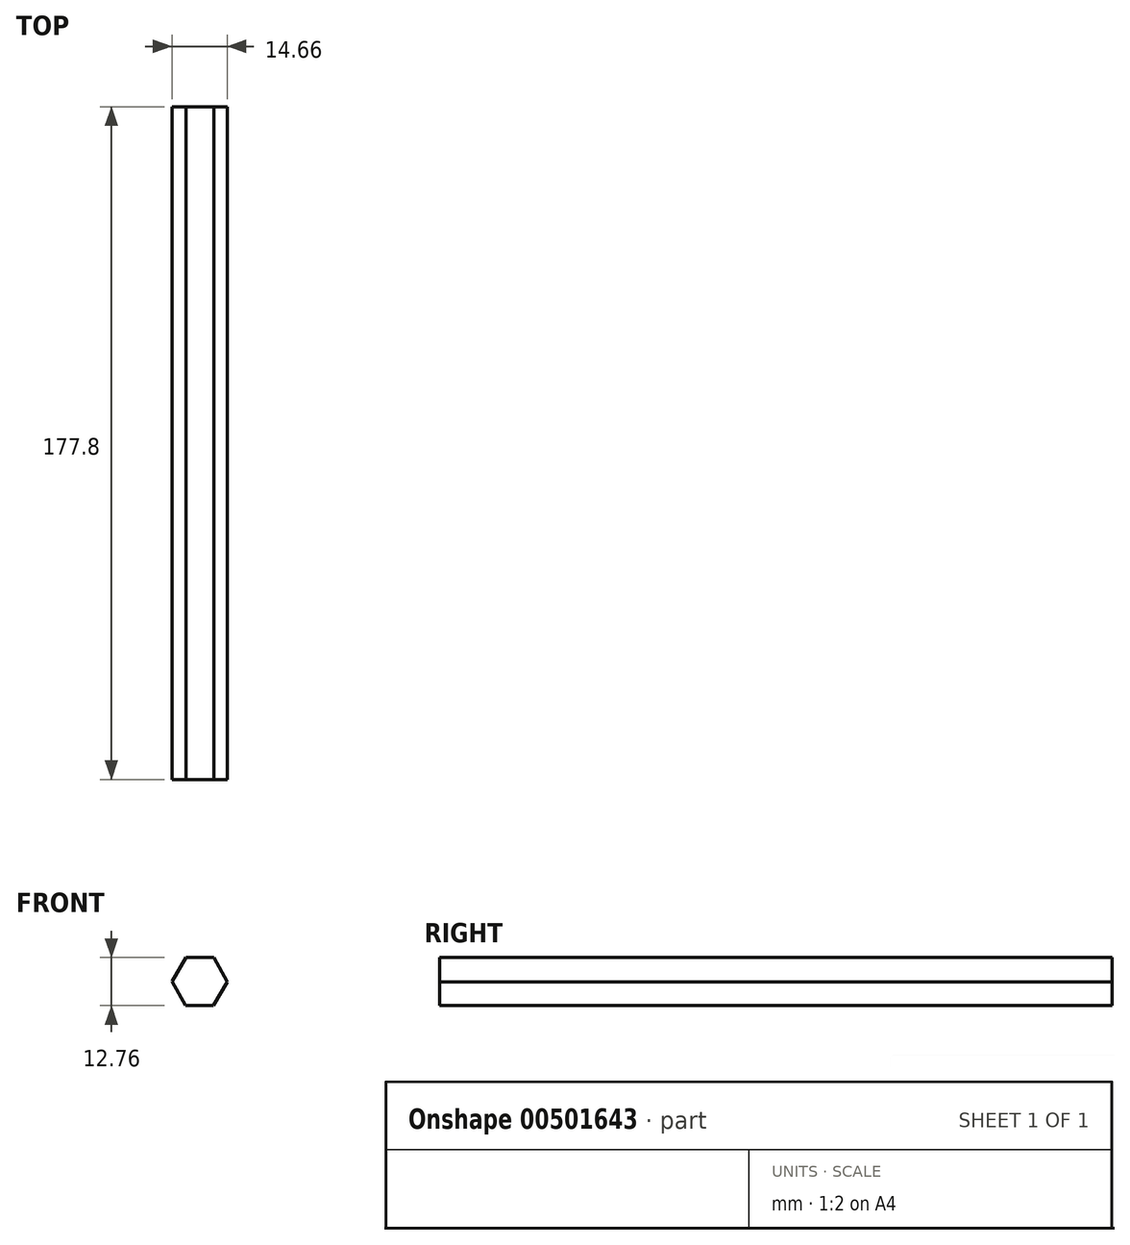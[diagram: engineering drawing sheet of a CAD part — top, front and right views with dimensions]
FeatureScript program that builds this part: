
annotation { "Feature Type Name" : "Feature", "Feature Type Description" : "" }
export const myFeature = defineFeature(function(context is Context, id is Id, definition is map)
    precondition{}
    {
        {
            var Q0;
            Q0=qCreatedBy(makeId("Front.planeOp"),FACE);
            var sketch = newSketch(context, id + "F0", { "sketchPlane" : qUnion([Q0])});
            skCircle(sketch, "E0.cCircle", {"center": v(0, 0) * mm, "radius": 6.35 * mm, "construction": true});
            skLineSegment(sketch, "E0.0", {"start": v(3.73, 6.32) * mm, "end": v(7.33, -0.07) * mm});
            skLineSegment(sketch, "E0.1", {"start": v(7.33, -0.07) * mm, "end": v(3.6, -6.38) * mm});
            skLineSegment(sketch, "E0.2", {"start": v(3.6, -6.38) * mm, "end": v(-3.73, -6.32) * mm});
            skLineSegment(sketch, "E0.3", {"start": v(-3.73, -6.32) * mm, "end": v(-7.33, 0.07) * mm});
            skLineSegment(sketch, "E0.4", {"start": v(-7.33, 0.07) * mm, "end": v(-3.6, 6.38) * mm});
            skLineSegment(sketch, "E0.5", {"start": v(-3.6, 6.38) * mm, "end": v(3.73, 6.32) * mm});
            skPoint(sketch, "E0.0.midPoint", {"position": v(5.53, 3.12) * mm});
            skSolve(sketch);
        }
        {
            var Q0;
            Q0=qSketchRegion(id+"F0",true);
            extrude(context, id + "F1", {"entities" : qUnion([Q0]), "depth" : 177.8 * mm});
        }
    });
